# Revit family: Sanitary_Basins_Roca_THE-GAP-450-In-countertop
name_source: partatom
category: Plumbing Fixtures
units: mm (PartAtom-declared; Revit-internal decimal feet)

## family parameters
Always vertical = No
Cut with Voids When Loaded = No
OmniClass Number = 23.45.00.00
OmniClass Title = Sanitary, Laundry, and Cleaning Equipment
Part Type = Normal
Room Calculation Point = No
Round Connector Dimension = Use Diameter
Shared = No
Work Plane-Based = Yes

## types (1)
- THE GAP 450 In countertop vitreous china basin
    BIMobject category = Basins
    BIMobject category code = sanitary-basins
    BIMobject main category = Sanitary
    BIMobject main category code = sanitary
    BOSUseNativeGeometries = 1
    Brand url = http://www.roca.es
    Default Elevation = 1219 mm
    Edition number = 1
    IFC Classification = Sanitary Terminal
    Manufacturer name = Roca
    Masterformat 2014 Code = 22 41 16.16
    Masterformat 2014 Description = Residential Sinks
    NBS Reference Code = 35-65-70-94
    NBS Reference Description = Wash Basin Systems
    OmniClass Code = 23-31 13 00
    OmniClass Description = Sinks
    Product Guid = 65856ef2-0d2f-4b8f-9161-540521972ed0
    Product SKU = 32747YxxR
    Product data url = https://bimobject.com
    QR code = http://bimobject.com
    Uniclass 1.4 Code = L7212
    Uniclass 1.4 Description = Washbasins
    Uniclass 2.0 Code = SS-35-65-70-94
    Uniclass 2.0 Description = Wash Basin Systems
    Uniclass 2015 Code = Pr_40_20_96
    Uniclass 2015 Name = Wash basins, sinks and troughs
    Uniformat II Code = D2010
    Uniformat II Description = Plumbing Fixtures

## geometry (parser evidence)
native form markers: Sweep x3
no freeform markers — native parametric forms only
